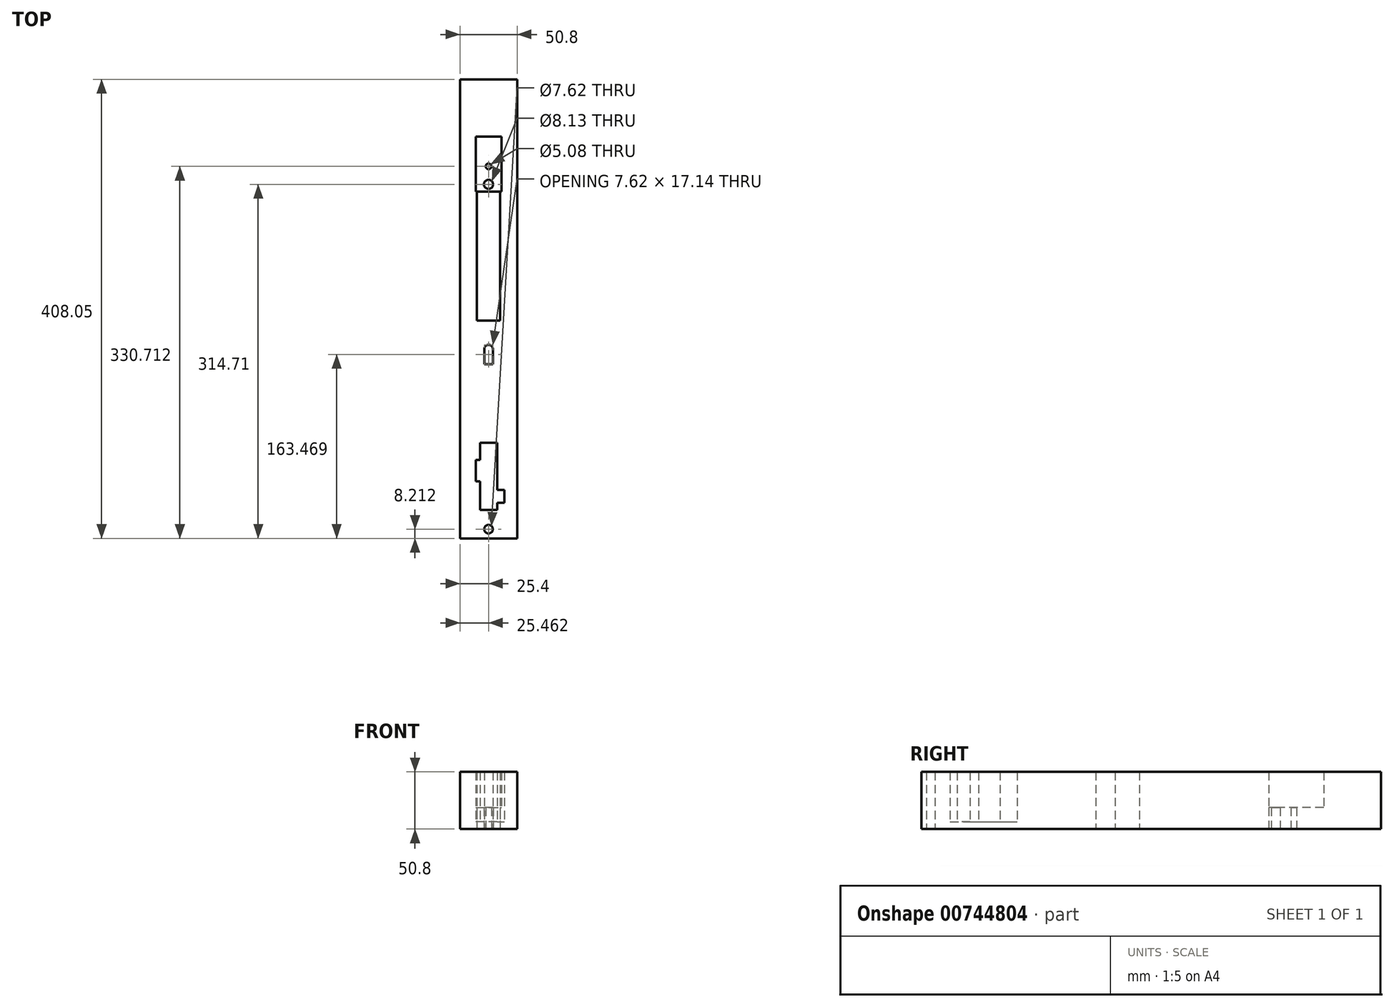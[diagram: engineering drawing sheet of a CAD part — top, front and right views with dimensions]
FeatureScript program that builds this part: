
annotation { "Feature Type Name" : "Feature", "Feature Type Description" : "" }
export const myFeature = defineFeature(function(context is Context, id is Id, definition is map)
    precondition{}
    {
        {
            var Q0;
            Q0=qCreatedBy(makeId("Top.planeOp"),FACE);
            var sketch = newSketch(context, id + "F0", { "sketchPlane" : qUnion([Q0])});
            skLineSegment(sketch, "E0", {"start": v(0, 122.48) * mm, "end": v(-10.35, 122.48) * mm});
            skLineSegment(sketch, "E1", {"start": v(0, 122.48) * mm, "end": v(10.35, 122.48) * mm});
            skLineSegment(sketch, "E2", {"start": v(-10.35, 122.48) * mm, "end": v(-10.35, 237.16) * mm});
            skLineSegment(sketch, "E3", {"start": v(-10.35, 237.16) * mm, "end": v(10.35, 237.16) * mm});
            skLineSegment(sketch, "E4", {"start": v(10.35, 237.16) * mm, "end": v(10.35, 122.48) * mm});
            skLineSegment(sketch, "E5", {"start": v(0.06, -45.8) * mm, "end": v(-7.56, -45.8) * mm});
            skLineSegment(sketch, "E6", {"start": v(-7.56, -45.8) * mm, "end": v(7.68, -45.8) * mm});
            skLineSegment(sketch, "E7", {"start": v(7.68, 13.9) * mm, "end": v(-7.56, 13.9) * mm});
            skCircle(sketch, "E8", {"center": v(0, -62.99) * mm, "radius": 3.81 * mm});
            skCircle(sketch, "E9", {"center": v(0, 243.5) * mm, "radius": 4.06 * mm});
            skCircle(sketch, "E10", {"center": v(0, 259.51) * mm, "radius": 2.54 * mm});
            skLineSegment(sketch, "E11", {"start": v(-11.43, 237.16) * mm, "end": v(-10.35, 237.16) * mm});
            skLineSegment(sketch, "E12", {"start": v(0, 286.05) * mm, "end": v(11.43, 286.05) * mm});
            skLineSegment(sketch, "E13", {"start": v(11.43, 286.05) * mm, "end": v(11.43, 237.16) * mm});
            skLineSegment(sketch, "E14", {"start": v(11.43, 237.16) * mm, "end": v(10.35, 237.16) * mm});
            skLineSegment(sketch, "E15", {"start": v(0, 286.05) * mm, "end": v(-11.43, 286.05) * mm});
            skLineSegment(sketch, "E16", {"start": v(-11.43, 286.05) * mm, "end": v(-11.43, 237.16) * mm});
            skLineSegment(sketch, "E17", {"start": v(7.68, -28.06) * mm, "end": v(14.03, -28.06) * mm});
            skLineSegment(sketch, "E18", {"start": v(14.03, -28.06) * mm, "end": v(14.03, -39.5) * mm});
            skLineSegment(sketch, "E19", {"start": v(14.03, -39.5) * mm, "end": v(7.68, -39.5) * mm});
            skLineSegment(sketch, "E20", {"start": v(0, -71.2) * mm, "end": v(-25.4, -71.2) * mm});
            skLineSegment(sketch, "E21", {"start": v(-25.4, -71.2) * mm, "end": v(-25.4, 336.85) * mm});
            skLineSegment(sketch, "E22", {"start": v(0, -71.2) * mm, "end": v(25.4, -71.2) * mm});
            skLineSegment(sketch, "E23", {"start": v(25.4, -71.2) * mm, "end": v(25.4, 336.85) * mm});
            skLineSegment(sketch, "E24", {"start": v(25.4, 336.85) * mm, "end": v(-25.4, 336.85) * mm});
            skLineSegment(sketch, "E25", {"start": v(7.68, -45.8) * mm, "end": v(7.68, -39.5) * mm});
            skLineSegment(sketch, "E26", {"start": v(7.68, -28.06) * mm, "end": v(7.68, 13.9) * mm});
            skLineSegment(sketch, "E27", {"start": v(-7.56, -45.8) * mm, "end": v(-7.56, -20.4) * mm});
            skLineSegment(sketch, "E28", {"start": v(-7.56, -20.4) * mm, "end": v(-11.37, -20.4) * mm});
            skLineSegment(sketch, "E29", {"start": v(-7.56, -20.4) * mm, "end": v(-7.56, -45.8) * mm});
            skLineSegment(sketch, "E30", {"start": v(-11.37, -20.4) * mm, "end": v(-11.37, -1.35) * mm});
            skLineSegment(sketch, "E31", {"start": v(-11.37, -1.35) * mm, "end": v(-7.56, -1.35) * mm});
            skLineSegment(sketch, "E32", {"start": v(-7.56, -1.35) * mm, "end": v(-7.56, 13.9) * mm});
            skLineSegment(sketch, "E33", {"start": v(0, -59.18) * mm, "end": v(0.06, 93.22) * mm});
            skCircle(sketch, "E34", {"center": v(0.06, 97.03) * mm, "radius": 3.8 * mm});
            skLineSegment(sketch, "E35", {"start": v(3.87, 97.03) * mm, "end": v(3.87, 83.7) * mm});
            skLineSegment(sketch, "E36", {"start": v(-3.75, 97.03) * mm, "end": v(-3.75, 83.7) * mm});
            skLineSegment(sketch, "E37", {"start": v(-3.75, 83.7) * mm, "end": v(3.87, 83.7) * mm});
            skSolve(sketch);
        }
        {
            var Q0;
            Q0=makeQuery(id+"F0.imprint","IMPRINT",FACE,{"disambiguationData":[TD([[makeQuery(id+"F0.imprint","IMPRINT",EDGE,{"derivedFrom":sQuery(id+"F0.wireOp",EDGE,"E0")}),1.0]])]});
            extrude(context, id + "F1", {"entities" : qUnion([Q0]), "depth" : 50.8 * mm, "offsetDistance" : 25.4 * mm});
        }
        {
            var Q0;
            Q0=makeQuery(id+"F0.imprint","IMPRINT",FACE,{"disambiguationData":[TD([[makeQuery(id+"F0.imprint","IMPRINT",EDGE,{"derivedFrom":sQuery(id+"F0.wireOp",EDGE,"E3")}),1.0]])]});
            extrude(context, id + "F2", {"entities" : qUnion([Q0]), "operationType" : NewBodyOperationType.ADD, "depth" : 19.05 * mm, "offsetDistance" : 25.4 * mm});
        }
        {
            var Q0;
            Q0=makeQuery(id+"F0.imprint","IMPRINT",FACE,{"disambiguationData":[TD([[makeQuery(id+"F0.imprint","IMPRINT",EDGE,{"derivedFrom":sQuery(id+"F0.wireOp",EDGE,"E7")}),1.0]])]});
            extrude(context, id + "F3", {"entities" : qUnion([Q0]), "operationType" : NewBodyOperationType.ADD, "depth" : 6.35 * mm, "offsetDistance" : 25.4 * mm});
        }
        {
            var Q0;
            Q0=makeQuery(id+"F0.imprint","IMPRINT",FACE,{"disambiguationData":[TD([[makeQuery(id+"F0.imprint","IMPRINT",EDGE,{"derivedFrom":sQuery(id+"F0.wireOp",EDGE,"E28")}),-1.0]])]});
            extrude(context, id + "F4", {"entities" : qUnion([Q0]), "operationType" : NewBodyOperationType.ADD, "depth" : 6.35 * mm, "offsetDistance" : 25.4 * mm});
        }
        {
            var Q0;
            Q0=makeQuery(id+"F0.imprint","IMPRINT",FACE,{"disambiguationData":[TD([[makeQuery(id+"F0.imprint","IMPRINT",EDGE,{"derivedFrom":sQuery(id+"F0.wireOp",EDGE,"E17")}),-1.0]])]});
            extrude(context, id + "F5", {"entities" : qUnion([Q0]), "operationType" : NewBodyOperationType.ADD, "depth" : 6.35 * mm, "offsetDistance" : 25.4 * mm});
        }
    });
